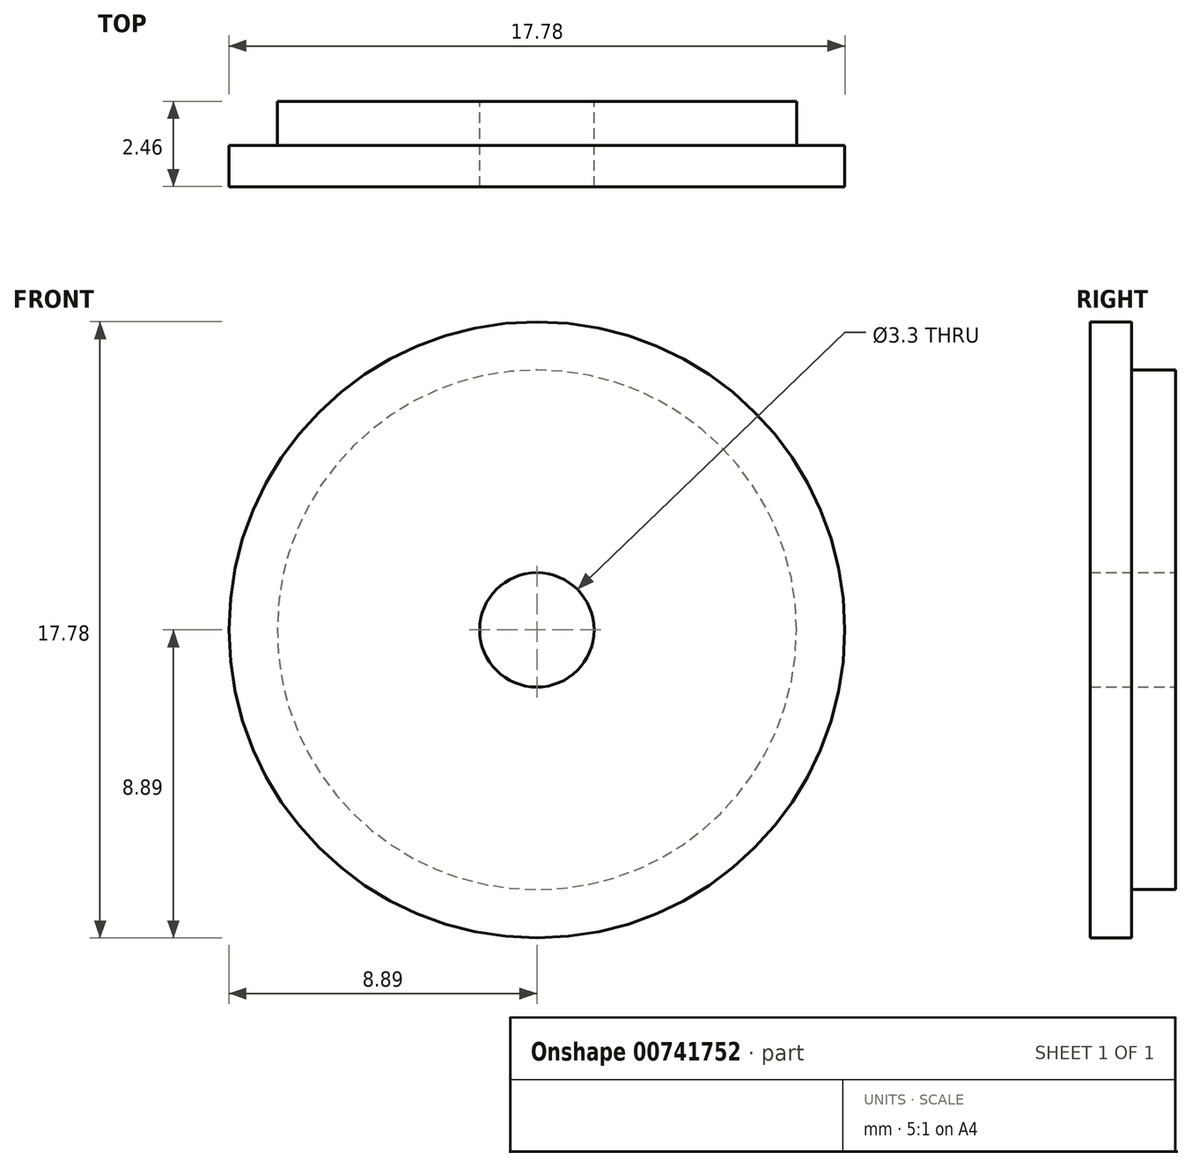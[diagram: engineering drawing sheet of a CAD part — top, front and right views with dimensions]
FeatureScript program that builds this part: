
annotation { "Feature Type Name" : "Feature", "Feature Type Description" : "" }
export const myFeature = defineFeature(function(context is Context, id is Id, definition is map)
    precondition{}
    {
        {
            var Q0;
            Q0=qCreatedBy(makeId("Front.planeOp"),FACE);
            var sketch = newSketch(context, id + "F0", { "sketchPlane" : qUnion([Q0])});
            skCircle(sketch, "E0", {"center": v(0, 0) * mm, "radius": 7.5 * mm});
            skCircle(sketch, "E1", {"center": v(0, 0) * mm, "radius": 1.65 * mm});
            skSolve(sketch);
        }
        {
            var Q0;
            Q0=makeQuery(id+"F0.imprint","IMPRINT",FACE,{"disambiguationData":[TD([[makeQuery(id+"F0.imprint","IMPRINT",EDGE,{"derivedFrom":sQuery(id+"F0.wireOp",EDGE,"E0")}),1.0]])]});
            extrude(context, id + "F1", {"entities" : qUnion([Q0]), "depth" : 1.2 * mm, "offsetDistance" : 25.4 * mm});
        }
        {
            var Q0;
            Q0=makeQuery(id+"F1.opExtrude","CAP_FACE",FACE,{"disambiguationData":[OSD([sQuery(id+"F0.wireOp",EDGE,"E0"),sQuery(id+"F0.wireOp",EDGE,"E1")])],"isStart":false});
            extrude(context, id + "F2", {"entities" : qUnion([Q0]), "operationType" : NewBodyOperationType.ADD, "depth" : 1.27 * mm, "offsetDistance" : 25.4 * mm});
        }
        {
            var Q0;
            Q0=makeQuery(id+"F2.opExtrude","CAP_FACE",FACE,{"disambiguationData":[OSD([sQuery(id+"F0.wireOp",EDGE,"E0"),sQuery(id+"F0.wireOp",EDGE,"E1")])],"isStart":false});
            var sketch = newSketch(context, id + "F3", { "sketchPlane" : qUnion([Q0])});
            skCircle(sketch, "E2", {"center": v(0, 0) * mm, "radius": 8.89 * mm});
            skSolve(sketch);
        }
        {
            var Q0;
            Q0=makeQuery(id+"F3.imprint","IMPRINT",FACE,{"disambiguationData":[TD([[makeQuery(id+"F3.imprint","IMPRINT",EDGE,{"derivedFrom":sQuery(id+"F3.wireOp",EDGE,"E2")}),1.0]])]});
            extrude(context, id + "F4", {"entities" : qUnion([Q0]), "operationType" : NewBodyOperationType.ADD, "oppositeDirection" : true, "depth" : 1.2 * mm, "offsetDistance" : 25.4 * mm});
        }
    });
